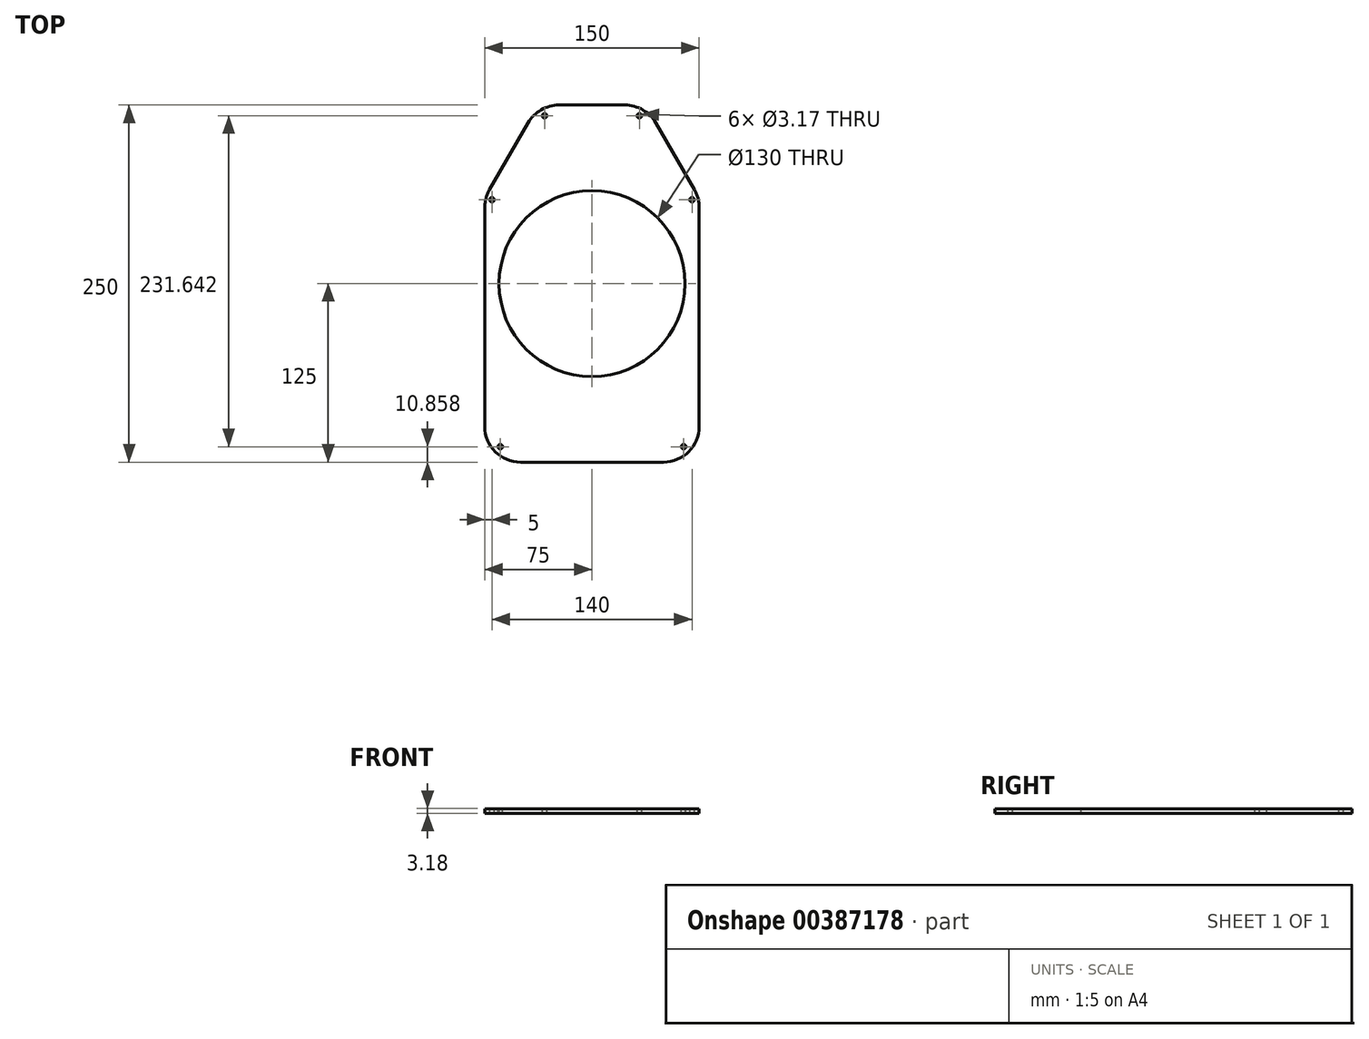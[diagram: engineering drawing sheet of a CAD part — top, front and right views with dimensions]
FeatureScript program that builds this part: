
annotation { "Feature Type Name" : "Feature", "Feature Type Description" : "" }
export const myFeature = defineFeature(function(context is Context, id is Id, definition is map)
    precondition{}
    {
        {
            var Q0;
            Q0=qCreatedBy(makeId("Top.planeOp"),FACE);
            var sketch = newSketch(context, id + "F0", { "sketchPlane" : qUnion([Q0])});
            skLineSegment(sketch, "E0", {"start": v(-75, -125) * mm, "end": v(75, -125) * mm});
            skLineSegment(sketch, "E1", {"start": v(75, -125) * mm, "end": v(75, 60.05) * mm});
            skLineSegment(sketch, "E2", {"start": v(75, 60.05) * mm, "end": v(37.5, 125) * mm});
            skLineSegment(sketch, "E3", {"start": v(37.5, 125) * mm, "end": v(-37.5, 125) * mm});
            skLineSegment(sketch, "E4", {"start": v(-37.5, 125) * mm, "end": v(-75, 60.05) * mm});
            skLineSegment(sketch, "E5", {"start": v(-75, 60.05) * mm, "end": v(-75, -125) * mm});
            skPoint(sketch, "E6.visualSharp", {"position": v(-75, -125) * mm});
            skPoint(sketch, "E7.visualSharp", {"position": v(75, -125) * mm});
            skLineSegment(sketch, "E8", {"start": v(0, 125) * mm, "end": v(0, -125) * mm, "construction": true});
            skCircle(sketch, "E9", {"center": v(0, 0) * mm, "radius": 65 * mm});
            skSolve(sketch);
        }
        {
            var Q0;
            Q0=makeQuery(id+"F0.imprint","IMPRINT",FACE,{"disambiguationData":[TD([[makeQuery(id+"F0.imprint","IMPRINT",EDGE,{"derivedFrom":sQuery(id+"F0.wireOp",EDGE,"E0")}),1.0]])]});
            extrude(context, id + "F1", {"entities" : qUnion([Q0]), "depth" : 3.17 * mm});
        }
        {
            var Q0;
            Q0=makeQuery(id+"F1.opExtrude","SWEPT_EDGE",EDGE,{"disambiguationData":[OSD([sQuery(id+"F0.wireOp",EDGE,"E0"),sQuery(id+"F0.wireOp",EDGE,"E5")])]});
            var Q1;
            Q1=makeQuery(id+"F1.opExtrude","SWEPT_EDGE",EDGE,{"disambiguationData":[OSD([sQuery(id+"F0.wireOp",EDGE,"E0"),sQuery(id+"F0.wireOp",EDGE,"E1")])]});
            var Q2;
            Q2=makeQuery(id+"F1.opExtrude","SWEPT_EDGE",EDGE,{"disambiguationData":[OSD([sQuery(id+"F0.wireOp",EDGE,"E3"),sQuery(id+"F0.wireOp",EDGE,"E4")])]});
            var Q3;
            Q3=makeQuery(id+"F1.opExtrude","SWEPT_EDGE",EDGE,{"disambiguationData":[OSD([sQuery(id+"F0.wireOp",EDGE,"E4"),sQuery(id+"F0.wireOp",EDGE,"E5")])]});
            var Q4;
            Q4=makeQuery(id+"F1.opExtrude","SWEPT_EDGE",EDGE,{"disambiguationData":[OSD([sQuery(id+"F0.wireOp",EDGE,"E1"),sQuery(id+"F0.wireOp",EDGE,"E2")])]});
            var Q5;
            Q5=makeQuery(id+"F1.opExtrude","SWEPT_EDGE",EDGE,{"disambiguationData":[OSD([sQuery(id+"F0.wireOp",EDGE,"E2"),sQuery(id+"F0.wireOp",EDGE,"E3")])]});
            fillet(context, id + "F2", {"entities" : qUnion([Q0, Q1, Q2, Q3, Q4, Q5]), "radius" : 25 * mm, "tangentPropagation" : true, "allowEdgeOverflow" : false});
        }
        {
            var Q0;
            Q0=makeQuery(id+"F1.opExtrude","CAP_FACE",FACE,{"disambiguationData":[OSD([sQuery(id+"F0.wireOp",EDGE,"E0"),sQuery(id+"F0.wireOp",EDGE,"E1"),sQuery(id+"F0.wireOp",EDGE,"E2"),sQuery(id+"F0.wireOp",EDGE,"E3"),sQuery(id+"F0.wireOp",EDGE,"E4"),sQuery(id+"F0.wireOp",EDGE,"E5"),sQuery(id+"F0.wireOp",EDGE,"f97b5YFU-O6pF-mwI3-0pcH-pPvOokoEmqy7"),sQuery(id+"F0.wireOp",EDGE,"CfihZrcp-4kWP-pYRo-7GKS-K6kYaTdg3Hfn"),sQuery(id+"F0.wireOp",EDGE,"sRlby8dM-M6pS-v9B2-HMKG-o1kvIz38uoyo"),sQuery(id+"F0.wireOp",EDGE,"5FsD2HY8-ilj8-puNg-WOoj-e2pKw8DwUl8K"),sQuery(id+"F0.wireOp",EDGE,"Sq9dvODw-BmSl-nNyv-AY4i-KjPGw3QQGqai"),sQuery(id+"F0.wireOp",EDGE,"KuzzBzD0-NJGa-LiR3-iS1d-QWDL3pI3iYqA"),sQuery(id+"F0.wireOp",EDGE,"ujkRF9Fo-wLAz-2l24-DYOw-OwzvOPzSW11X"),sQuery(id+"F0.wireOp",EDGE,"2av6td6h-coQF-ggF9-FM7I-AnsYqIXI4VQc"),sQuery(id+"F0.wireOp",EDGE,"ibLPYZLi-B5Xk-2sKE-twix-TcULawOpbV7i"),sQuery(id+"F0.wireOp",EDGE,"d68435e1-0e8f-463b-9315-39ed8a1cdd6c.trimOffspring"),sQuery(id+"F0.wireOp",EDGE,"c2135ded-43d6-46e9-b4b3-af269b061847.trimOffspring"),sQuery(id+"F0.wireOp",EDGE,"eae176ab-f3d7-4957-b22e-1193cbf2c76c.trimOffspring"),sQuery(id+"F0.wireOp",EDGE,"5lcR4Beo-DAwb-zem0-jxSY-UTAuiQeu7I8N"),sQuery(id+"F0.wireOp",EDGE,"49f12868-44d0-44c0-8b6c-6b708f740ba6.trimOffspring"),sQuery(id+"F0.wireOp",EDGE,"5918f2cd-d373-437f-9af0-729bed35f3ad.trimOffspring"),sQuery(id+"F0.wireOp",EDGE,"4fcfa271-db52-4476-bc53-1cf0bbe3a6bd.trimOffspring")])],"isStart":false});
            var sketch = newSketch(context, id + "F3", { "sketchPlane" : qUnion([Q0])});
            skCircle(sketch, "E10", {"center": v(-64.14, -114.14) * mm, "radius": 1.59 * mm});
            skCircle(sketch, "E11", {"center": v(64.14, -114.14) * mm, "radius": 1.59 * mm});
            skCircle(sketch, "E12", {"center": v(70, 58.7) * mm, "radius": 1.59 * mm});
            skCircle(sketch, "E13", {"center": v(-70, 58.7) * mm, "radius": 1.59 * mm});
            skCircle(sketch, "E14", {"center": v(33.17, 117.5) * mm, "radius": 1.59 * mm});
            skCircle(sketch, "E15", {"center": v(-33.17, 117.5) * mm, "radius": 1.59 * mm});
            skLineSegment(sketch, "E16", {"start": v(-64.14, -114.14) * mm, "end": v(-67.68, -117.68) * mm, "construction": true});
            skLineSegment(sketch, "E17", {"start": v(64.14, -114.14) * mm, "end": v(67.68, -117.68) * mm, "construction": true});
            skSolve(sketch);
        }
        {
            var Q0;
            Q0=makeQuery(id+"F3.imprint","IMPRINT",FACE,{"disambiguationData":[TD([[makeQuery(id+"F3.imprint","IMPRINT",EDGE,{"derivedFrom":sQuery(id+"F3.wireOp",EDGE,"E15")}),1.0]])]});
            var Q1;
            Q1=makeQuery(id+"F3.imprint","IMPRINT",FACE,{"disambiguationData":[TD([[makeQuery(id+"F3.imprint","IMPRINT",EDGE,{"derivedFrom":sQuery(id+"F3.wireOp",EDGE,"E14")}),1.0]])]});
            var Q2;
            Q2=makeQuery(id+"F3.imprint","IMPRINT",FACE,{"disambiguationData":[TD([[makeQuery(id+"F3.imprint","IMPRINT",EDGE,{"derivedFrom":sQuery(id+"F3.wireOp",EDGE,"E12")}),1.0]])]});
            var Q3;
            Q3=makeQuery(id+"F3.imprint","IMPRINT",FACE,{"disambiguationData":[TD([[makeQuery(id+"F3.imprint","IMPRINT",EDGE,{"derivedFrom":sQuery(id+"F3.wireOp",EDGE,"E13")}),1.0]])]});
            var Q4;
            Q4=makeQuery(id+"F3.imprint","IMPRINT",FACE,{"disambiguationData":[TD([[makeQuery(id+"F3.imprint","IMPRINT",EDGE,{"derivedFrom":sQuery(id+"F3.wireOp",EDGE,"E10")}),1.0]])]});
            var Q5;
            Q5=makeQuery(id+"F3.imprint","IMPRINT",FACE,{"disambiguationData":[TD([[makeQuery(id+"F3.imprint","IMPRINT",EDGE,{"derivedFrom":sQuery(id+"F3.wireOp",EDGE,"E11")}),1.0]])]});
            extrude(context, id + "F4", {"entities" : qUnion([Q0, Q1, Q2, Q3, Q4, Q5]), "operationType" : NewBodyOperationType.REMOVE, "endBound" : BoundingType.THROUGH_ALL, "oppositeDirection" : true, "depth" : 25 * mm});
        }
    });
